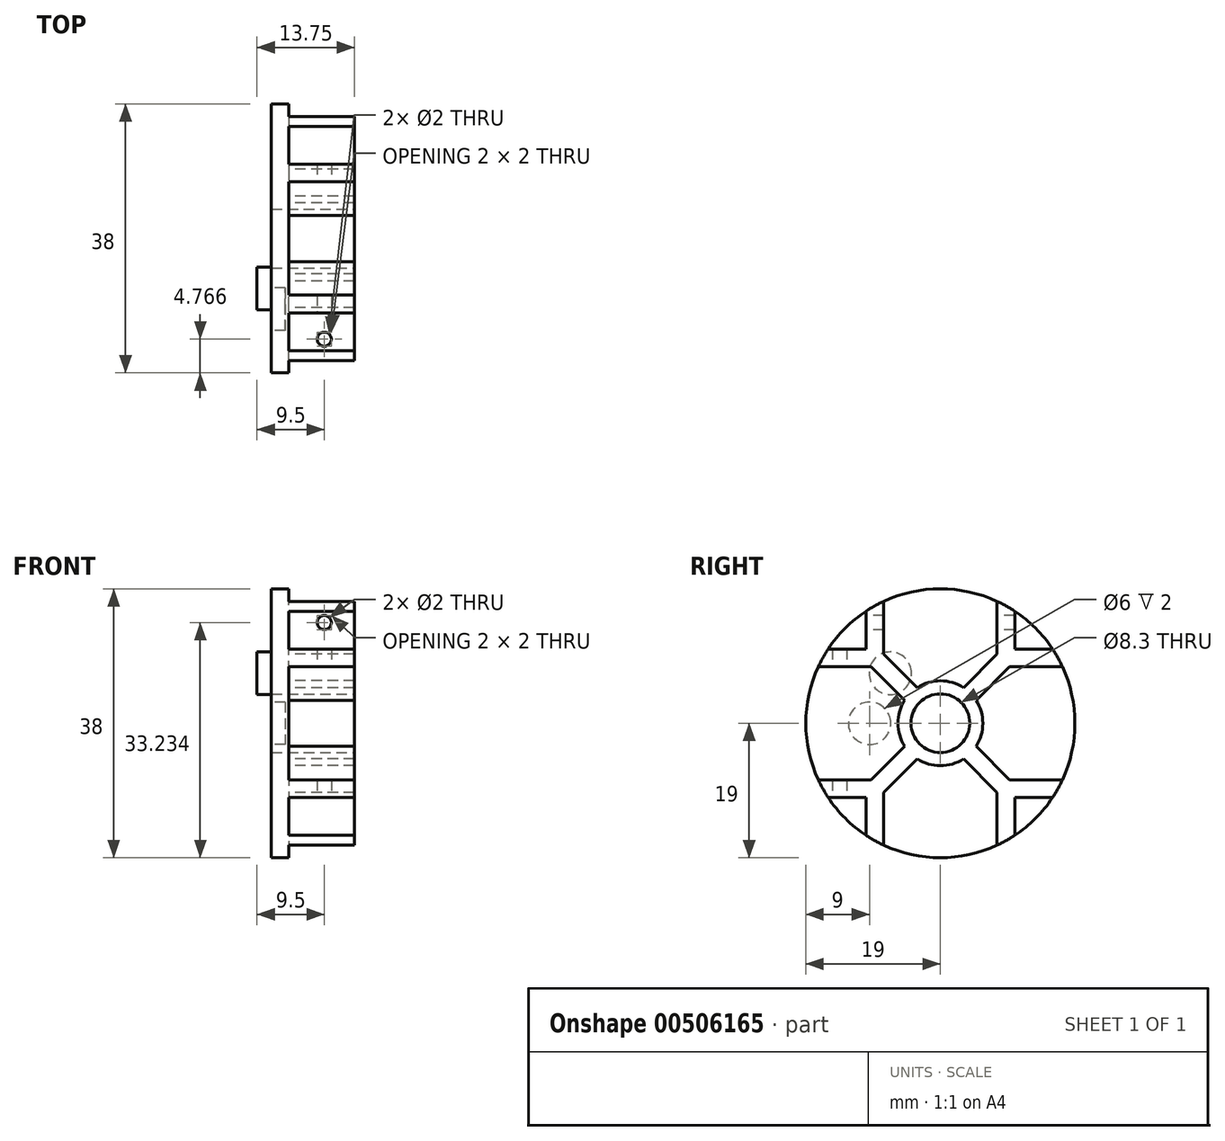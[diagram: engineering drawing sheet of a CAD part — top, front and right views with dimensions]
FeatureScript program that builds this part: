
annotation { "Feature Type Name" : "Feature", "Feature Type Description" : "" }
export const myFeature = defineFeature(function(context is Context, id is Id, definition is map)
    precondition{}
    {
        {
            var Q0;
            Q0=qCreatedBy(makeId("Right.planeOp"),FACE);
            var sketch = newSketch(context, id + "F0", { "sketchPlane" : qUnion([Q0])});
            skCircle(sketch, "E0", {"center": v(0, 0) * mm, "radius": 19 * mm});
            skSolve(sketch);
        }
        {
            var Q0;
            Q0=makeQuery(id+"F0.imprint","IMPRINT",FACE,{"disambiguationData":[TD([[makeQuery(id+"F0.imprint","IMPRINT",EDGE,{"derivedFrom":sQuery(id+"F0.wireOp",EDGE,"E0")}),1.0]])]});
            extrude(context, id + "F1", {"entities" : qUnion([Q0]), "depth" : 2.5 * mm});
        }
        {
            var Q0;
            Q0=makeQuery(id+"F1.opExtrude","CAP_FACE",FACE,{"disambiguationData":[OSD([sQuery(id+"F0.wireOp",EDGE,"E0")])],"isStart":false});
            var sketch = newSketch(context, id + "F2", { "sketchPlane" : qUnion([Q0])});
            skLineSegment(sketch, "E1", {"start": v(-10.5, 15.84) * mm, "end": v(-10.5, 10.5) * mm});
            skLineSegment(sketch, "E2", {"start": v(-10.5, 10.5) * mm, "end": v(-15.84, 10.5) * mm});
            skCircle(sketch, "E3.0", {"center": v(0, 0) * mm, "radius": 19 * mm});
            skCircle(sketch, "E4", {"center": v(0, 0) * mm, "radius": 6 * mm});
            skLineSegment(sketch, "E5", {"start": v(-17.23, 8) * mm, "end": v(-9.77, 8) * mm});
            skLineSegment(sketch, "E6", {"start": v(-9.77, 8) * mm, "end": v(-5.03, 3.27) * mm});
            skLineSegment(sketch, "E7", {"start": v(-3.27, 5.03) * mm, "end": v(-8, 9.77) * mm});
            skLineSegment(sketch, "E8", {"start": v(-8, 9.77) * mm, "end": v(-8, 17.23) * mm});
            skPoint(sketch, "E9", {"position": v(0, 20.25) * mm});
            skLineSegment(sketch, "E10.MirrorCS", {"start": v(8, 9.77) * mm, "end": v(8, 17.23) * mm});
            skLineSegment(sketch, "E11.MirrorCS", {"start": v(3.27, 5.03) * mm, "end": v(8, 9.77) * mm});
            skLineSegment(sketch, "E12.MirrorCS", {"start": v(9.77, 8) * mm, "end": v(5.03, 3.27) * mm});
            skLineSegment(sketch, "E13.MirrorCS", {"start": v(17.23, 8) * mm, "end": v(9.77, 8) * mm});
            skLineSegment(sketch, "E14.MirrorCS", {"start": v(10.5, 10.5) * mm, "end": v(15.84, 10.5) * mm});
            skLineSegment(sketch, "E15.MirrorCS", {"start": v(10.5, 15.84) * mm, "end": v(10.5, 10.5) * mm});
            skLineSegment(sketch, "E16.MirrorCS", {"start": v(-17.23, -8) * mm, "end": v(-9.77, -8) * mm});
            skLineSegment(sketch, "E17.MirrorCS", {"start": v(-10.5, -10.5) * mm, "end": v(-15.84, -10.5) * mm});
            skLineSegment(sketch, "E18.MirrorCS", {"start": v(-10.5, -15.84) * mm, "end": v(-10.5, -10.5) * mm});
            skLineSegment(sketch, "E19.MirrorCS", {"start": v(-8, -9.77) * mm, "end": v(-8, -17.23) * mm});
            skLineSegment(sketch, "E20.MirrorCS", {"start": v(-3.27, -5.03) * mm, "end": v(-8, -9.77) * mm});
            skLineSegment(sketch, "E21.MirrorCS", {"start": v(-9.77, -8) * mm, "end": v(-5.03, -3.27) * mm});
            skLineSegment(sketch, "E22.MirrorCS", {"start": v(3.27, -5.03) * mm, "end": v(8, -9.77) * mm});
            skLineSegment(sketch, "E23.MirrorCS", {"start": v(8, -9.77) * mm, "end": v(8, -17.23) * mm});
            skLineSegment(sketch, "E24.MirrorCS", {"start": v(10.5, -15.84) * mm, "end": v(10.5, -10.5) * mm});
            skLineSegment(sketch, "E25.MirrorCS", {"start": v(10.5, -10.5) * mm, "end": v(15.84, -10.5) * mm});
            skLineSegment(sketch, "E26.MirrorCS", {"start": v(17.23, -8) * mm, "end": v(9.77, -8) * mm});
            skLineSegment(sketch, "E27.MirrorCS", {"start": v(9.77, -8) * mm, "end": v(5.03, -3.27) * mm});
            skSolve(sketch);
        }
        {
            var Q0;
            {var subQ3=sQuery(id+"F2.wireOp",EDGE,"E1");Q0=makeQuery(id+"F2.imprint","IMPRINT",FACE,{"disambiguationData":[TD([[makeQuery(id+"F2.imprint","IMPRINT",EDGE,{"derivedFrom":subQ3}),1.0]])]});}
            var Q1;
            {var subQ0=sQuery(id+"F2.wireOp",EDGE,"E4");var subQ4=makeQuery(id+"F2.imprint","INTERSECT",VERTEX,{"derivedFrom":[subQ0,sQuery(id+"F2.wireOp",EDGE,"E11.MirrorCS")]});Q1=makeQuery(id+"F2.imprint","IMPRINT",FACE,{"disambiguationData":[TD([[makeQuery(id+"F2.imprint","IMPRINT",EDGE,{"disambiguationData":[TD([[subQ4,1.0]])],"derivedFrom":subQ0}),1.0]])]});}
            var Q2;
            {var subQ0=sQuery(id+"F2.wireOp",EDGE,"E10.MirrorCS");Q2=makeQuery(id+"F2.imprint","IMPRINT",FACE,{"disambiguationData":[TD([[makeQuery(id+"F2.imprint","IMPRINT",EDGE,{"derivedFrom":subQ0}),-1.0]])]});}
            var Q3;
            {var subQ0=sQuery(id+"F2.wireOp",EDGE,"E22.MirrorCS");Q3=makeQuery(id+"F2.imprint","IMPRINT",FACE,{"disambiguationData":[TD([[makeQuery(id+"F2.imprint","IMPRINT",EDGE,{"derivedFrom":subQ0}),1.0]])]});}
            var Q4;
            {var subQ0=sQuery(id+"F2.wireOp",EDGE,"E16.MirrorCS");Q4=makeQuery(id+"F2.imprint","IMPRINT",FACE,{"disambiguationData":[TD([[makeQuery(id+"F2.imprint","IMPRINT",EDGE,{"derivedFrom":subQ0}),-1.0]])]});}
            extrude(context, id + "F3", {"entities" : qUnion([Q0, Q1, Q2, Q3, Q4]), "operationType" : NewBodyOperationType.ADD, "depth" : 9.25 * mm});
        }
        {
            var Q0;
            Q0=makeQuery(id+"F3.opExtrude","SWEPT_FACE",FACE,{"disambiguationData":[OSD([sQuery(id+"F2.wireOp",EDGE,"E8")])]});
            var sketch = newSketch(context, id + "F4", { "sketchPlane" : qUnion([Q0])});
            skCircle(sketch, "E28", {"center": v(-7.5, 14.23) * mm, "radius": 1 * mm});
            skSolve(sketch);
        }
        {
            var Q0;
            Q0=makeQuery(id+"F4.imprint","IMPRINT",FACE,{"disambiguationData":[TD([[makeQuery(id+"F4.imprint","IMPRINT",EDGE,{"derivedFrom":sQuery(id+"F4.wireOp",EDGE,"E28")}),1.0]])]});
            extrude(context, id + "F5", {"entities" : qUnion([Q0]), "operationType" : NewBodyOperationType.REMOVE, "endBound" : BoundingType.SYMMETRIC, "depth" : 40 * mm});
        }
        {
            var Q0;
            Q0=makeQuery(id+"F3.opExtrude","SWEPT_FACE",FACE,{"disambiguationData":[OSD([sQuery(id+"F2.wireOp",EDGE,"E5")])]});
            var sketch = newSketch(context, id + "F6", { "sketchPlane" : qUnion([Q0])});
            skCircle(sketch, "E29", {"center": v(7.5, 14.23) * mm, "radius": 1 * mm});
            skSolve(sketch);
        }
        {
            var Q0;
            Q0=makeQuery(id+"F6.imprint","IMPRINT",FACE,{"disambiguationData":[TD([[makeQuery(id+"F6.imprint","IMPRINT",EDGE,{"derivedFrom":sQuery(id+"F6.wireOp",EDGE,"E29")}),1.0]])]});
            extrude(context, id + "F7", {"entities" : qUnion([Q0]), "operationType" : NewBodyOperationType.REMOVE, "endBound" : BoundingType.SYMMETRIC, "oppositeDirection" : true, "depth" : 40 * mm});
        }
        {
            var Q0;
            Q0=makeQuery(id+"F1.opExtrude","CAP_FACE",FACE,{"disambiguationData":[OSD([sQuery(id+"F0.wireOp",EDGE,"E0")])],"isStart":true});
            var sketch = newSketch(context, id + "F8", { "sketchPlane" : qUnion([Q0])});
            skCircle(sketch, "E30", {"center": v(10, 0) * mm, "radius": 3 * mm});
            skCircle(sketch, "E31", {"center": v(7.07, 7.07) * mm, "radius": 3 * mm});
            skLineSegment(sketch, "E32", {"start": v(0, 0) * mm, "end": v(7.07, 7.07) * mm, "construction": true});
            skSolve(sketch);
        }
        {
            var Q0;
            Q0=makeQuery(id+"F8.imprint","IMPRINT",FACE,{"disambiguationData":[TD([[makeQuery(id+"F8.imprint","IMPRINT",EDGE,{"derivedFrom":sQuery(id+"F8.wireOp",EDGE,"E31")}),1.0]])]});
            extrude(context, id + "F9", {"entities" : qUnion([Q0]), "operationType" : NewBodyOperationType.ADD, "depth" : 2 * mm});
        }
        {
            var Q0;
            Q0=makeQuery(id+"F8.imprint","IMPRINT",FACE,{"disambiguationData":[TD([[makeQuery(id+"F8.imprint","IMPRINT",EDGE,{"derivedFrom":sQuery(id+"F8.wireOp",EDGE,"E30")}),1.0]])]});
            extrude(context, id + "F10", {"entities" : qUnion([Q0]), "operationType" : NewBodyOperationType.REMOVE, "oppositeDirection" : true, "depth" : 2 * mm});
        }
        {
            var Q0;
            Q0=makeQuery(id+"F3.opExtrude","CAP_FACE",FACE,{"disambiguationData":[OSD([sQuery(id+"F2.wireOp",EDGE,"E1"),sQuery(id+"F2.wireOp",EDGE,"E2"),sQuery(id+"F2.wireOp",EDGE,"E3.0"),sQuery(id+"F2.wireOp",EDGE,"E4"),sQuery(id+"F2.wireOp",EDGE,"E5"),sQuery(id+"F2.wireOp",EDGE,"E6"),sQuery(id+"F2.wireOp",EDGE,"E7"),sQuery(id+"F2.wireOp",EDGE,"E8"),sQuery(id+"F2.wireOp",EDGE,"E10.MirrorCS"),sQuery(id+"F2.wireOp",EDGE,"E11.MirrorCS"),sQuery(id+"F2.wireOp",EDGE,"E12.MirrorCS"),sQuery(id+"F2.wireOp",EDGE,"E13.MirrorCS"),sQuery(id+"F2.wireOp",EDGE,"E14.MirrorCS"),sQuery(id+"F2.wireOp",EDGE,"E15.MirrorCS"),sQuery(id+"F2.wireOp",EDGE,"E16.MirrorCS"),sQuery(id+"F2.wireOp",EDGE,"E17.MirrorCS"),sQuery(id+"F2.wireOp",EDGE,"E18.MirrorCS"),sQuery(id+"F2.wireOp",EDGE,"E19.MirrorCS"),sQuery(id+"F2.wireOp",EDGE,"E20.MirrorCS"),sQuery(id+"F2.wireOp",EDGE,"E21.MirrorCS"),sQuery(id+"F2.wireOp",EDGE,"E22.MirrorCS"),sQuery(id+"F2.wireOp",EDGE,"E23.MirrorCS"),sQuery(id+"F2.wireOp",EDGE,"E24.MirrorCS"),sQuery(id+"F2.wireOp",EDGE,"E25.MirrorCS"),sQuery(id+"F2.wireOp",EDGE,"E26.MirrorCS"),sQuery(id+"F2.wireOp",EDGE,"E27.MirrorCS")])],"isStart":false});
            var sketch = newSketch(context, id + "F11", { "sketchPlane" : qUnion([Q0])});
            skCircle(sketch, "E33", {"center": v(0, 0) * mm, "radius": 4.15 * mm});
            skSolve(sketch);
        }
        {
            var Q0;
            Q0=makeQuery(id+"F11.imprint","IMPRINT",FACE,{"disambiguationData":[TD([[makeQuery(id+"F11.imprint","IMPRINT",EDGE,{"derivedFrom":sQuery(id+"F11.wireOp",EDGE,"E33")}),1.0]])]});
            extrude(context, id + "F12", {"entities" : qUnion([Q0]), "operationType" : NewBodyOperationType.REMOVE, "endBound" : BoundingType.UP_TO_NEXT, "oppositeDirection" : true, "depth" : 25 * mm});
        }
    });
